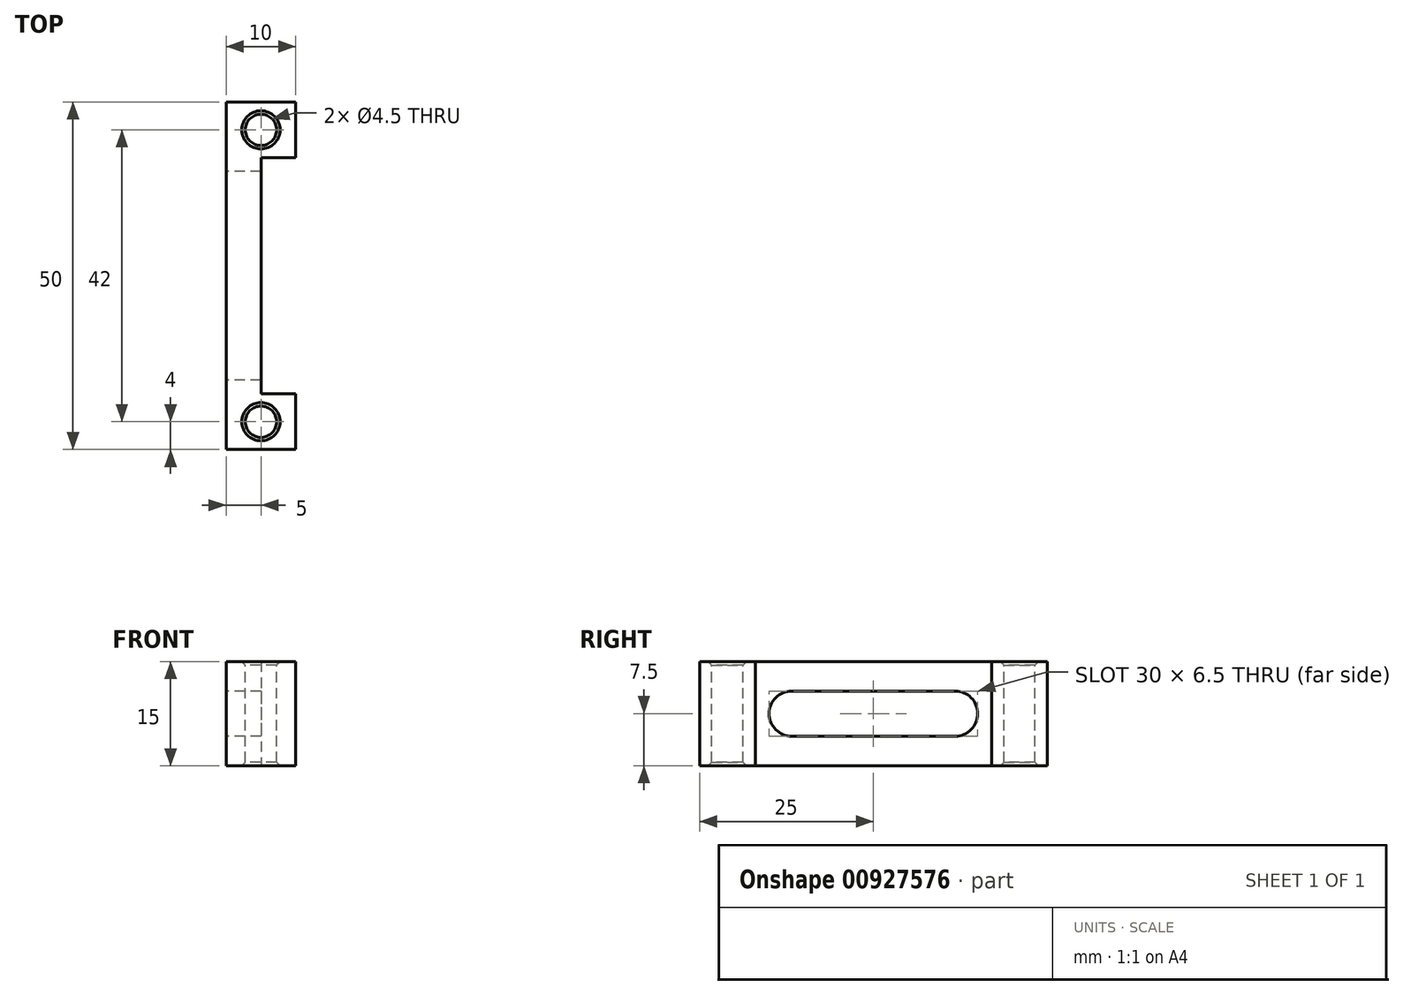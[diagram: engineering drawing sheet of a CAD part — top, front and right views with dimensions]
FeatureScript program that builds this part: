
annotation { "Feature Type Name" : "Feature", "Feature Type Description" : "" }
export const myFeature = defineFeature(function(context is Context, id is Id, definition is map)
    precondition{}
    {
        {
            var Q0;
            Q0=qCreatedBy(makeId("Right.planeOp"),FACE);
            var sketch = newSketch(context, id + "F0", { "sketchPlane" : qUnion([Q0])});
            skLineSegment(sketch, "E0", {"start": v(-43.44, 0) * mm, "end": v(35.89, 0) * mm, "construction": true});
            skLineSegment(sketch, "E1", {"start": v(-50, 7.5) * mm, "end": v(0, 7.5) * mm});
            skLineSegment(sketch, "E2", {"start": v(0, 7.5) * mm, "end": v(0, 0) * mm});
            skLineSegment(sketch, "E3", {"start": v(-50, 7.5) * mm, "end": v(-50, 3.25) * mm});
            skLineSegment(sketch, "E4", {"start": v(-36.75, 3.25) * mm, "end": v(-13.25, 3.25) * mm});
            skLineSegment(sketch, "E5", {"start": v(-50, 3.25) * mm, "end": v(-50, 0) * mm});
            skLineSegment(sketch, "E6.MirrorCS", {"start": v(-36.75, -3.25) * mm, "end": v(-13.25, -3.25) * mm});
            skLineSegment(sketch, "E7.MirrorCS", {"start": v(0, -7.5) * mm, "end": v(0, 0) * mm});
            skLineSegment(sketch, "E8.MirrorCS", {"start": v(-50, -7.5) * mm, "end": v(0, -7.5) * mm});
            skLineSegment(sketch, "E9.MirrorCS", {"start": v(-50, -7.5) * mm, "end": v(-50, -3.25) * mm});
            skLineSegment(sketch, "E10.MirrorCS", {"start": v(-50, -3.25) * mm, "end": v(-50, 0) * mm});
            skArc(sketch, "E11", {"start": v(-36.75, 3.25) * mm, "mid": v(-40, 0) * mm, "end": v(-36.75, -3.25) * mm});
            skArc(sketch, "E12", {"start": v(-13.25, -3.25) * mm, "mid": v(-10, 0) * mm, "end": v(-13.25, 3.25) * mm});
            skLineSegment(sketch, "E13", {"start": v(-36.75, 10.18) * mm, "end": v(-36.75, -14.87) * mm, "construction": true});
            skSolve(sketch);
        }
        {
            var Q0;
            Q0=makeQuery(id+"F0.imprint","IMPRINT",FACE,{"disambiguationData":[TD([[makeQuery(id+"F0.imprint","IMPRINT",EDGE,{"derivedFrom":sQuery(id+"F0.wireOp",EDGE,"E1")}),-1.0]])]});
            extrude(context, id + "F1", {"entities" : qUnion([Q0]), "depth" : 10 * mm, "offsetDistance" : 25 * mm});
        }
        {
            var Q0;
            Q0=makeQuery(id+"F1.opExtrude","CAP_FACE",FACE,{"disambiguationData":[OSD([sQuery(id+"F0.wireOp",EDGE,"E1"),sQuery(id+"F0.wireOp",EDGE,"E2"),sQuery(id+"F0.wireOp",EDGE,"E3"),sQuery(id+"F0.wireOp",EDGE,"E4"),sQuery(id+"F0.wireOp",EDGE,"8NzZxl9S-CZfl-iixf-eZWp-nfnbeH51dhmg"),sQuery(id+"F0.wireOp",EDGE,"OWshbWAj-bpf3-3sTe-xLN1-rTfrItKx2rCg"),sQuery(id+"F0.wireOp",EDGE,"E5"),sQuery(id+"F0.wireOp",EDGE,"E6.MirrorCS"),sQuery(id+"F0.wireOp",EDGE,"d16fd012-3ffa-4aef-b742-8a998a697e7d0.MirrorCS"),sQuery(id+"F0.wireOp",EDGE,"fcd14ed7-aec7-42df-8f76-806a2d8f2c290.MirrorCS"),sQuery(id+"F0.wireOp",EDGE,"E7.MirrorCS"),sQuery(id+"F0.wireOp",EDGE,"E8.MirrorCS"),sQuery(id+"F0.wireOp",EDGE,"E9.MirrorCS"),sQuery(id+"F0.wireOp",EDGE,"E10.MirrorCS")])],"isStart":false});
            var sketch = newSketch(context, id + "F2", { "sketchPlane" : qUnion([Q0])});
            skLineSegment(sketch, "E14.bottom", {"start": v(-42, 7.5) * mm, "end": v(-8, 7.5) * mm});
            skLineSegment(sketch, "E14.top", {"start": v(-42, -7.5) * mm, "end": v(-8, -7.5) * mm});
            skLineSegment(sketch, "E14.right", {"start": v(-8, 7.5) * mm, "end": v(-8, -7.5) * mm});
            skLineSegment(sketch, "E15", {"start": v(-42, 13.6) * mm, "end": v(-42, -14.64) * mm, "construction": true});
            skLineSegment(sketch, "E16", {"start": v(-42, 7.5) * mm, "end": v(-42, -7.5) * mm});
            skSolve(sketch);
        }
        {
            var Q0;
            Q0 = qSketchRegion(id + "F2", true);
            extrude(context, id + "F3", {"entities" : qUnion([Q0]), "operationType" : NewBodyOperationType.REMOVE, "oppositeDirection" : true, "depth" : 5 * mm, "offsetDistance" : 25 * mm});
        }
        {
            var Q0;
            Q0=makeQuery(id+"F1.opExtrude","SWEPT_FACE",FACE,{"disambiguationData":[OSD([sQuery(id+"F0.wireOp",EDGE,"E1")])]});
            var sketch = newSketch(context, id + "F4", { "sketchPlane" : qUnion([Q0])});
            skLineSegment(sketch, "E17", {"start": v(15.92, -46) * mm, "end": v(-3.25, -46) * mm, "construction": true});
            skPoint(sketch, "E17.startSnap0", {"position": v(10, -46) * mm});
            skCircle(sketch, "E18", {"center": v(5, -46) * mm, "radius": 2.25 * mm});
            skPoint(sketch, "E19.startSnap0", {"position": v(5, 0) * mm});
            skLineSegment(sketch, "E20", {"start": v(-11.07, -25) * mm, "end": v(27.19, -25) * mm, "construction": true});
            skPoint(sketch, "E20.startSnap0", {"position": v(0, -25) * mm});
            skCircle(sketch, "E21.MirrorC", {"center": v(5, -4) * mm, "radius": 2.25 * mm});
            skLineSegment(sketch, "E22", {"start": v(5, 5.33) * mm, "end": v(5, -52.5) * mm, "construction": true});
            skSolve(sketch);
        }
        {
            var Q0;
            Q0 = qSketchRegion(id + "F4", true);
            extrude(context, id + "F5", {"entities" : qUnion([Q0]), "operationType" : NewBodyOperationType.REMOVE, "oppositeDirection" : true, "depth" : 25 * mm, "offsetDistance" : 25 * mm});
        }
        {
            var Q0;
            Q0=makeQuery(id+"F5.boolean.opBoolean","COPY",FACE,{"derivedFrom":makeQuery(id+"F5.opExtrude","SWEPT_FACE",FACE,{"disambiguationData":[OSD([sQuery(id+"F4.wireOp",EDGE,"E18")])]})});
            var Q1;
            Q1=makeQuery(id+"F5.boolean.opBoolean","COPY",FACE,{"derivedFrom":makeQuery(id+"F5.opExtrude","SWEPT_FACE",FACE,{"disambiguationData":[OSD([sQuery(id+"F4.wireOp",EDGE,"E21.MirrorC")])]})});
            chamfer(context, id + "F6", {"entities" : qUnion([Q0, Q1]), "width" : 0.5 * mm, "tangentPropagation" : true});
        }
    });
